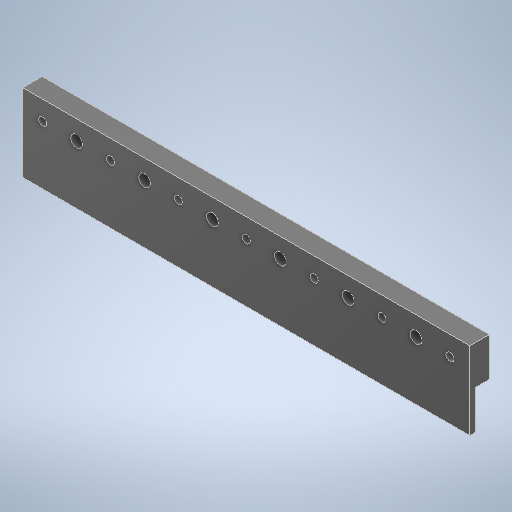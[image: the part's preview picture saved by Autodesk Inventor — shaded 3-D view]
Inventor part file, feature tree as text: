
AUTODESK INVENTOR PART (.ipt)
format: ipt  version: 2025.1 (Build 291241020, 241B)  size: 633,344 bytes
history: native  units: mm
features: sketch x5, extrude x3, hole x2, pattern_linear x2, other x2, chamfer x1, reference x1
ambient origin geometry x8: Origin, YZ Plane, XZ Plane, XY Plane, X Axis, Y Axis, Z Axis, Center Point
bodies: Solid1 (feature_tree)
feature tree (16):
  extrude  "Extrusion1"  Depth=20.0mm
  sketch  "Sketch2"  dims[d2=3.0mm d3=0.0mm d31=10.0mm]
  extrude  "Extrusion3"  Depth=10.0mm
  hole  "Hole3"  [1 undecoded]
  hole  "Hole2"  [1 undecoded]
  pattern_linear  "Rectangular Pattern2"  Spacing1=10.0mm  [1 undecoded]
  pattern_linear  "Rectangular Pattern3"  Count1=6 Spacing1=34.925mm
  chamfer  "Chamfer1"  Distance=10.0mm
  extrude  "Extrusion4"  Depth=10.0mm TaperAngle=45.0deg
  sketch  "Sketch1"  dims[d0=230.0mm d1=20.0mm]
  reference  "Reference1"
  sketch  "Sketch5"  dims[d32=20.0mm d33=10.0mm d34=0.0mm]
  sketch  "Sketch6"  dims[d35=27.6875mm]
  sketch  "Sketch7"  dims[d39=6.0mm d40=6.0mm d41=4.0mm d42=2.0mm d43=90.0deg d44=8.0mm d45=20.594885mm d47=34.925mm d51=10.0mm d52=4.1mm d53=6.0mm d54=4.0mm d55=2.0mm d56=90.0deg d57=6.0mm d58=0.0mm d59=60.0mm d61=34.925mm d62=10.0mm d63=2.0mm d64=2.0mm d65=45.0deg d66=5.0mm d67=0.0mm d68=0.0mm d73=10.225mm d74=70.0mm d76=34.925mm d77=0.5mm d78=0.872665mm d79=0.5mm d80=0.872665mm]
  other  "MagDrop4.iam"
  other  "Connect4_RACK:1"
note: 3 required parameter values undecoded (feature->parameter linkage not recoverable at this tier; creation-order binding heuristic only, values carry confidence <= 0.55)
